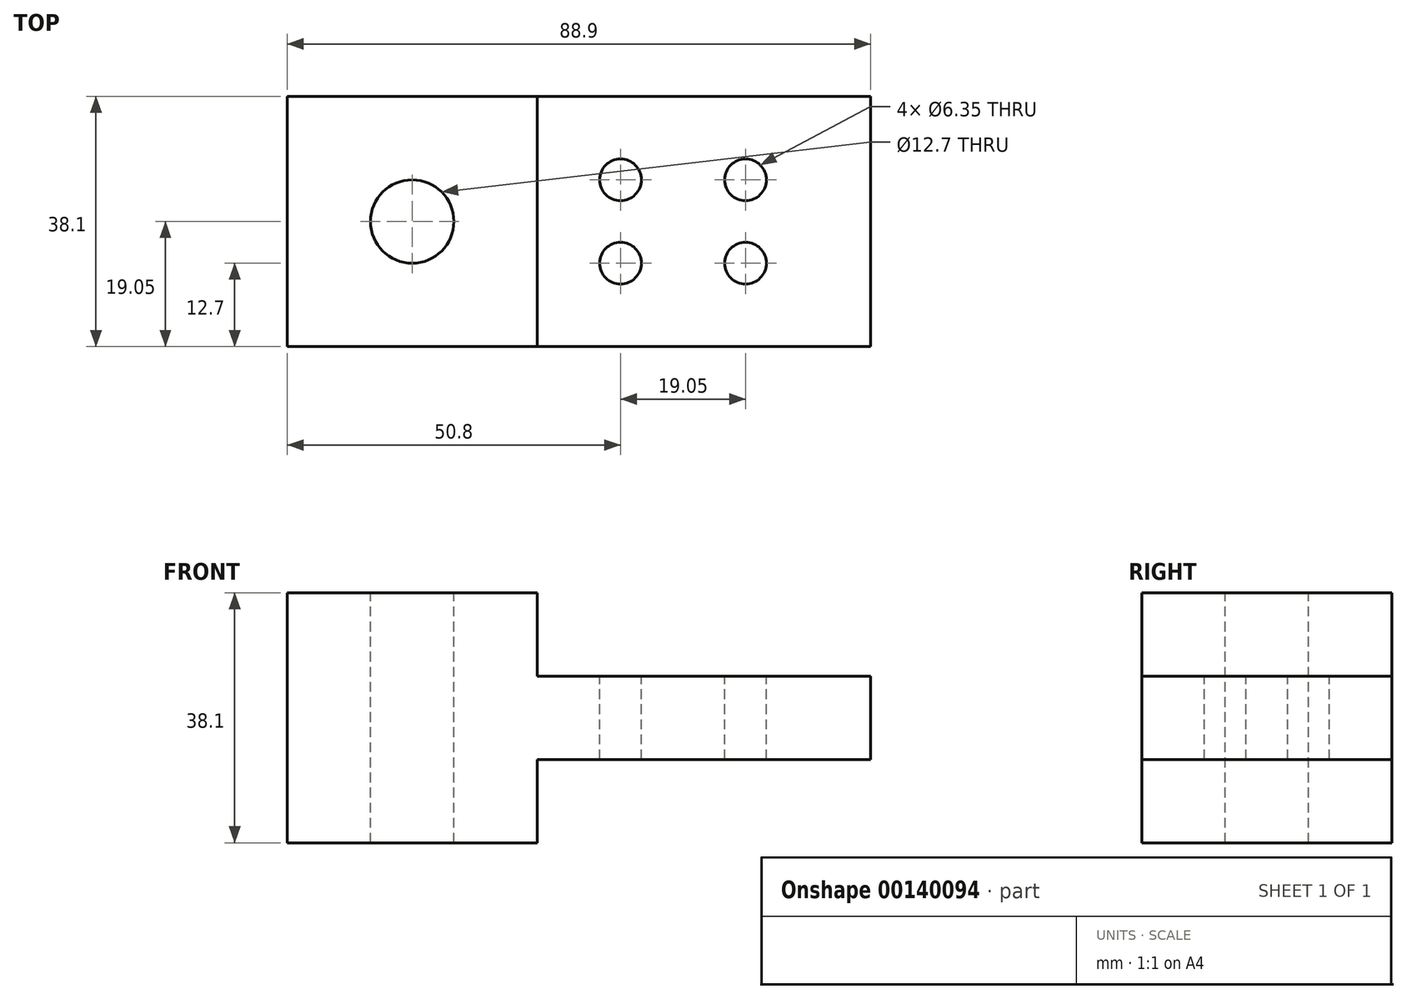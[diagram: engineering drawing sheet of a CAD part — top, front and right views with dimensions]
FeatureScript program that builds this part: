
annotation { "Feature Type Name" : "Feature", "Feature Type Description" : "" }
export const myFeature = defineFeature(function(context is Context, id is Id, definition is map)
    precondition{}
    {
        {
            var Q0;
            Q0=qCreatedBy(makeId("Front.planeOp"),FACE);
            var sketch = newSketch(context, id + "F0", { "sketchPlane" : qUnion([Q0])});
            skLineSegment(sketch, "E0", {"start": v(-34.02, 0) * mm, "end": v(116.02, 0) * mm, "construction": true});
            skLineSegment(sketch, "E1", {"start": v(0, 19.05) * mm, "end": v(0, -19.05) * mm});
            skLineSegment(sketch, "E2", {"start": v(0, 19.05) * mm, "end": v(38.1, 19.05) * mm});
            skLineSegment(sketch, "E3", {"start": v(38.1, 19.05) * mm, "end": v(38.1, 6.35) * mm});
            skLineSegment(sketch, "E4", {"start": v(38.1, 6.35) * mm, "end": v(88.9, 6.35) * mm});
            skLineSegment(sketch, "E5", {"start": v(88.9, 6.35) * mm, "end": v(88.9, -6.35) * mm});
            skLineSegment(sketch, "E6", {"start": v(88.9, -6.35) * mm, "end": v(38.1, -6.35) * mm});
            skLineSegment(sketch, "E7", {"start": v(38.1, -6.35) * mm, "end": v(38.1, -19.05) * mm});
            skLineSegment(sketch, "E8", {"start": v(38.1, -19.05) * mm, "end": v(0, -19.05) * mm});
            skSolve(sketch);
        }
        {
            var Q0;
            Q0=makeQuery(id+"F0.imprint","IMPRINT",FACE,{"disambiguationData":[TD([[makeQuery(id+"F0.imprint","IMPRINT",EDGE,{"derivedFrom":sQuery(id+"F0.wireOp",EDGE,"E1")}),1.0]])]});
            extrude(context, id + "F1", {"entities" : qUnion([Q0]), "endBound" : BoundingType.SYMMETRIC, "depth" : 38.1 * mm});
        }
        {
            var Q0;
            Q0=makeQuery(id+"F1.opExtrude","SWEPT_FACE",FACE,{"disambiguationData":[OSD([sQuery(id+"F0.wireOp",EDGE,"E2")])]});
            var sketch = newSketch(context, id + "F2", { "sketchPlane" : qUnion([Q0])});
            skCircle(sketch, "E9", {"center": v(19.05, 0) * mm, "radius": 6.35 * mm});
            skLineSegment(sketch, "E10", {"start": v(-3.03, 0) * mm, "end": v(99.2, 0) * mm, "construction": true});
            skPoint(sketch, "E10.endSnap0", {"position": v(38.1, 0) * mm});
            skCircle(sketch, "E11", {"center": v(50.8, 6.35) * mm, "radius": 3.18 * mm});
            skCircle(sketch, "E12", {"center": v(50.8, -6.35) * mm, "radius": 3.18 * mm});
            skCircle(sketch, "E13", {"center": v(69.85, 6.35) * mm, "radius": 3.18 * mm});
            skCircle(sketch, "E14", {"center": v(69.85, -6.35) * mm, "radius": 3.18 * mm});
            skSolve(sketch);
        }
        {
            var Q0;
            Q0=makeQuery(id+"F2.imprint","IMPRINT",FACE,{"disambiguationData":[TD([[makeQuery(id+"F2.imprint","IMPRINT",EDGE,{"derivedFrom":sQuery(id+"F2.wireOp",EDGE,"E9")}),1.0]])]});
            var Q1;
            Q1=makeQuery(id+"F2.imprint","IMPRINT",FACE,{"disambiguationData":[TD([[makeQuery(id+"F2.imprint","IMPRINT",EDGE,{"derivedFrom":sQuery(id+"F2.wireOp",EDGE,"E11")}),1.0]])]});
            var Q2;
            Q2=makeQuery(id+"F2.imprint","IMPRINT",FACE,{"disambiguationData":[TD([[makeQuery(id+"F2.imprint","IMPRINT",EDGE,{"derivedFrom":sQuery(id+"F2.wireOp",EDGE,"E12")}),1.0]])]});
            var Q3;
            Q3=makeQuery(id+"F2.imprint","IMPRINT",FACE,{"disambiguationData":[TD([[makeQuery(id+"F2.imprint","IMPRINT",EDGE,{"derivedFrom":sQuery(id+"F2.wireOp",EDGE,"E14")}),1.0]])]});
            var Q4;
            Q4=makeQuery(id+"F2.imprint","IMPRINT",FACE,{"disambiguationData":[TD([[makeQuery(id+"F2.imprint","IMPRINT",EDGE,{"derivedFrom":sQuery(id+"F2.wireOp",EDGE,"E13")}),1.0]])]});
            extrude(context, id + "F3", {"entities" : qUnion([Q0, Q1, Q2, Q3, Q4]), "operationType" : NewBodyOperationType.REMOVE, "endBound" : BoundingType.THROUGH_ALL, "oppositeDirection" : true, "depth" : 25.4 * mm});
        }
    });
